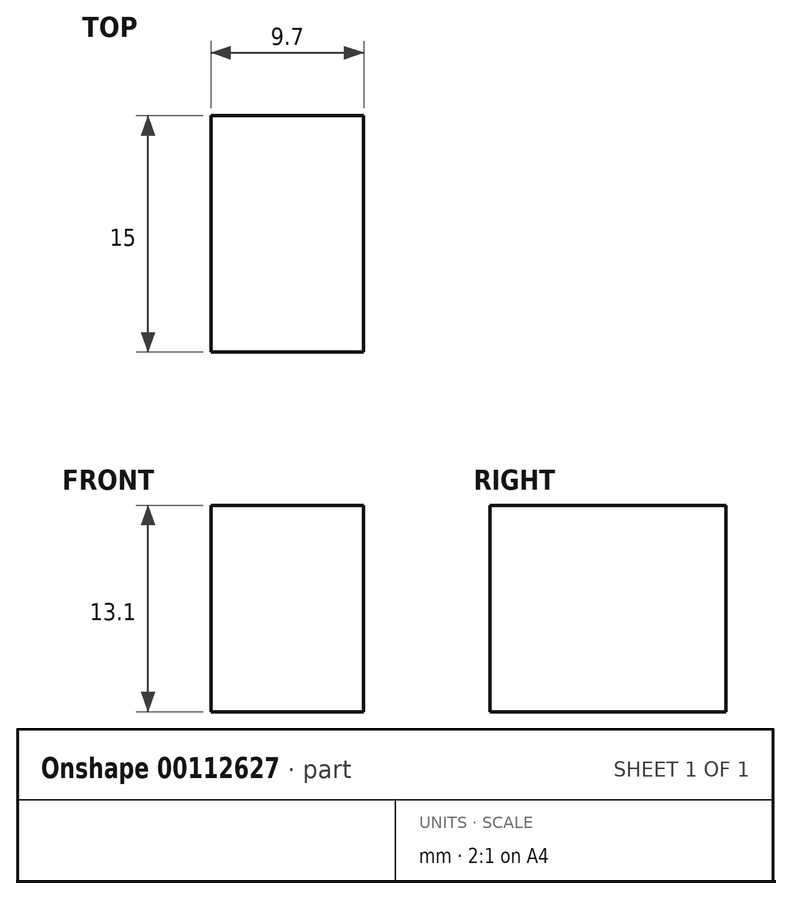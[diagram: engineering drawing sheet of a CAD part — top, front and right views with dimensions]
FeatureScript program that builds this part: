
annotation { "Feature Type Name" : "Feature", "Feature Type Description" : "" }
export const myFeature = defineFeature(function(context is Context, id is Id, definition is map)
    precondition{}
    {
        {
            var Q0;
            Q0=qCreatedBy(makeId("Front.planeOp"),FACE);
            var sketch = newSketch(context, id + "F0", { "sketchPlane" : qUnion([Q0])});
            skLineSegment(sketch, "E0.bottom", {"start": v(6.03, 6.42) * mm, "end": v(-3.67, 6.42) * mm});
            skLineSegment(sketch, "E0.top", {"start": v(6.03, -6.68) * mm, "end": v(-3.67, -6.68) * mm});
            skLineSegment(sketch, "E0.left", {"start": v(6.03, 6.42) * mm, "end": v(6.03, -6.68) * mm});
            skLineSegment(sketch, "E0.right", {"start": v(-3.67, 6.42) * mm, "end": v(-3.67, -6.68) * mm});
            skSolve(sketch);
        }
        {
            var Q0;
            Q0 = qSketchRegion(id + "F0", true);
            extrude(context, id + "F1", {"entities" : qUnion([Q0]), "endBound" : BoundingType.SYMMETRIC, "depth" : 15 * mm});
        }
    });
